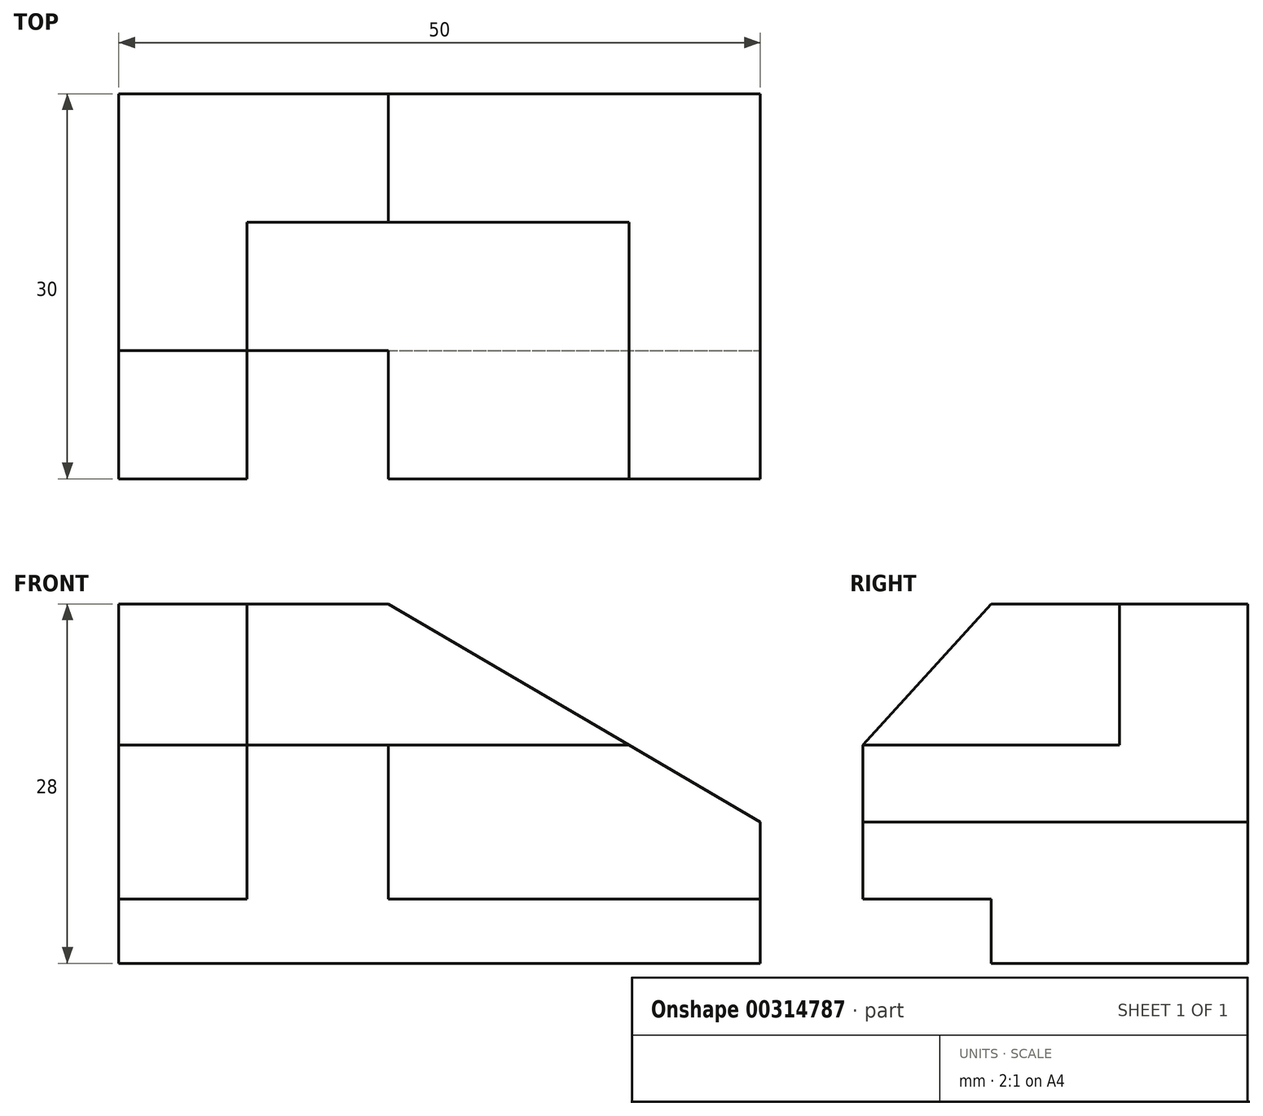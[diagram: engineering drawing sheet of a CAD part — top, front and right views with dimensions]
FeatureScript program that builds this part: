
annotation { "Feature Type Name" : "Feature", "Feature Type Description" : "" }
export const myFeature = defineFeature(function(context is Context, id is Id, definition is map)
    precondition{}
    {
        {
            var Q0;
            Q0=qCreatedBy(makeId("Front.planeOp"),FACE);
            var sketch = newSketch(context, id + "F0", { "sketchPlane" : qUnion([Q0])});
            skLineSegment(sketch, "E0.bottom", {"start": v(0, 0) * mm, "end": v(50, 0) * mm});
            skLineSegment(sketch, "E0.top", {"start": v(0, 28) * mm, "end": v(50, 28) * mm});
            skLineSegment(sketch, "E0.left", {"start": v(0, 0) * mm, "end": v(0, 28) * mm});
            skLineSegment(sketch, "E0.right", {"start": v(50, 0) * mm, "end": v(50, 28) * mm});
            skLineSegment(sketch, "E1", {"start": v(0, 5) * mm, "end": v(10, 5) * mm});
            skLineSegment(sketch, "E2.top", {"start": v(10, 17) * mm, "end": v(21, 17) * mm});
            skLineSegment(sketch, "E2.left", {"start": v(10, 5) * mm, "end": v(10, 17) * mm});
            skLineSegment(sketch, "E2.right", {"start": v(21, 5) * mm, "end": v(21, 17) * mm});
            skLineSegment(sketch, "E3", {"start": v(21, 28) * mm, "end": v(50, 11) * mm});
            skLineSegment(sketch, "E4", {"start": v(10, 17) * mm, "end": v(10, 28) * mm});
            skLineSegment(sketch, "E5", {"start": v(21, 17) * mm, "end": v(39.76, 17) * mm});
            skLineSegment(sketch, "E6.trimOffspring", {"start": v(21, 5) * mm, "end": v(50, 5) * mm});
            skSolve(sketch);
        }
        {
            var Q0;
            {var subQ0=sQuery(id+"F0.wireOp",EDGE,"E1");Q0=makeQuery(id+"F0.imprint","IMPRINT",FACE,{"disambiguationData":[TD([[makeQuery(id+"F0.imprint","IMPRINT",EDGE,{"derivedFrom":subQ0}),1.0]])]});}
            var Q1;
            {var subQ1=sQuery(id+"F0.wireOp",EDGE,"E0.bottom");Q1=makeQuery(id+"F0.imprint","IMPRINT",FACE,{"disambiguationData":[TD([[makeQuery(id+"F0.imprint","IMPRINT",EDGE,{"derivedFrom":subQ1}),1.0]])]});}
            var Q2;
            Q2=makeQuery(id+"F0.imprint","IMPRINT",FACE,{"disambiguationData":[TD([[makeQuery(id+"F0.imprint","IMPRINT",EDGE,{"derivedFrom":sQuery(id+"F0.wireOp",EDGE,"E2.right")}),-1.0]])]});
            var Q3;
            Q3=makeQuery(id+"F0.imprint","IMPRINT",FACE,{"disambiguationData":[TD([[makeQuery(id+"F0.imprint","IMPRINT",EDGE,{"derivedFrom":sQuery(id+"F0.wireOp",EDGE,"E2.top")}),1.0]])]});
            extrude(context, id + "F1", {"entities" : qUnion([Q0, Q1, Q2, Q3]), "oppositeDirection" : true, "depth" : 30 * mm});
        }
        {
            var Q0;
            {var subQ1=sQuery(id+"F0.wireOp",EDGE,"E0.bottom");Q0=makeQuery(id+"F0.imprint","IMPRINT",FACE,{"disambiguationData":[TD([[makeQuery(id+"F0.imprint","IMPRINT",EDGE,{"derivedFrom":subQ1}),1.0]])]});}
            extrude(context, id + "F2", {"entities" : qUnion([Q0]), "operationType" : NewBodyOperationType.REMOVE, "oppositeDirection" : true, "depth" : 10 * mm});
        }
        {
            var Q0;
            Q0=makeQuery(id+"F0.imprint","IMPRINT",FACE,{"disambiguationData":[TD([[makeQuery(id+"F0.imprint","IMPRINT",EDGE,{"derivedFrom":sQuery(id+"F0.wireOp",EDGE,"E2.top")}),1.0]])]});
            extrude(context, id + "F3", {"entities" : qUnion([Q0]), "operationType" : NewBodyOperationType.REMOVE, "oppositeDirection" : true, "depth" : 20 * mm});
        }
        {
            var Q0;
            Q0=makeQuery(id+"F3.boolean.opBoolean","MERGE",FACE,{"derivedFrom":[makeQuery(id+"F2.boolean.opBoolean","COPY",FACE,{"derivedFrom":makeQuery(id+"F2.opExtrude","SWEPT_FACE",FACE,{"disambiguationData":[OSD([sQuery(id+"F0.wireOp",EDGE,"E2.left")])]})}),makeQuery(id+"F3.opExtrude","SWEPT_FACE",FACE,{"disambiguationData":[OSD([sQuery(id+"F0.wireOp",EDGE,"E4")])]})]});
            var sketch = newSketch(context, id + "F4", { "sketchPlane" : qUnion([Q0])});
            skPoint(sketch, "E7.0", {"position": v(0, 17) * mm});
            skLineSegment(sketch, "E8", {"start": v(10, 28) * mm, "end": v(0, 17) * mm});
            skSolve(sketch);
        }
        {
            var Q0;
            {var subQ0=sQuery(id+"F4.wireOp",EDGE,"E8");Q0=makeQuery(id+"F4.imprint","IMPRINT",FACE,{"disambiguationData":[TD([[makeQuery(id+"F4.imprint","IMPRINT",EDGE,{"derivedFrom":subQ0}),-1.0]])]});}
            extrude(context, id + "F5", {"entities" : qUnion([Q0]), "operationType" : NewBodyOperationType.REMOVE, "endBound" : BoundingType.THROUGH_ALL, "oppositeDirection" : true, "depth" : 25 * mm});
        }
    });
